# Revit family: T93052 Indus ERAP LED_Tak
name_source: partatom
category: Lighting Fixtures
revit_build: Autodesk Revit 2016 (Build: 20160314_0715(x64)
units: mm (PartAtom-declared; Revit-internal decimal feet)

## family parameters
Always vertical = Yes
Cut with Voids When Loaded = No
Light Source = Yes
OmniClass Number = 23.80.70.11.21
OmniClass Title = Emergency Lighting
Part Type = Normal
Room Calculation Point = No
Round Connector Dimension = Use Diameter
Shared = No
Work Plane-Based = No

## types (8) — shared parameters
Apparent Load = 17 VA
Assembly Code = 4431
Body Material and Colour = Steel
Color Filter = 16777215
Dimming Lamp Color Temperature Shift = <None>
Emit Shape Visible in Rendering = No
Emit from Rectangle Length = 369 mm
Emit from Rectangle Width = 151 mm  [stored 0.495407 ft]
Height = 151 mm  [stored 0.495407 ft]
Height 1 = 111 mm  [stored 0.364173 ft]
Keynote = WT2
Lamp = 1
LedeLys = No
Length = 369 mm
Length 1 = 329 mm  [stored 1.0794 ft]
Manufacturer = Honeywell
MarkeringsLys = Yes
NS8360 = 4431_WT2
Number of Poles = 1
Photometric Web File = 20x42A12.ies
Tilt Angle = 90.00°
Type Comments = -UN
Voltage = 230 V
Wattage Comments = 17 W
Width = 112 mm  [stored 0.367454 ft]
zero-valued in all types: Height 2

## per-type parameters (varying)
| type | MarkeringsLys 45 Ned mot høyre | MarkeringsLys 45 Ned mot venstre | MarkeringsLys 45 Opp mot høyre | MarkeringsLys 45 Opp mot venstre | MarkeringsLys Høyre | MarkeringsLys Ned | MarkeringsLys Opp | MarkeringsLys Venstre | Markeringslys ikke normal | Markeringslys normal |
| MarkeringsLys (Ned) | No | No | No | No | No | Yes | No | No | No | Yes |
| MarkeringsLys (Opp) | No | No | No | No | No | No | Yes | No | No | Yes |
| MarkeringsLys (45 Ned mot høyre) | Yes | No | No | No | No | No | No | No | No | Yes |
| MarkeringsLys (45 Ned mot venstre) | No | Yes | No | No | No | No | No | No | Yes | No |
| MarkeringsLys (45 Opp mot høyre) | No | No | Yes | No | No | No | No | No | No | Yes |
| MarkeringsLys (45 Opp mot venstre) | No | No | No | Yes | No | No | No | No | Yes | No |
| MarkeringsLys (Høyre) | No | No | No | No | Yes | No | No | No | No | Yes |
| MarkeringsLys (Venstre) | No | No | No | No | No | No | No | Yes | Yes | No |

note: [stored X ft] marks values corroborated as IEEE doubles in the binary element streams (Revit-internal decimal feet)

## geometry (parser evidence)
native form markers: Sweep x21
no freeform markers — native parametric forms only
